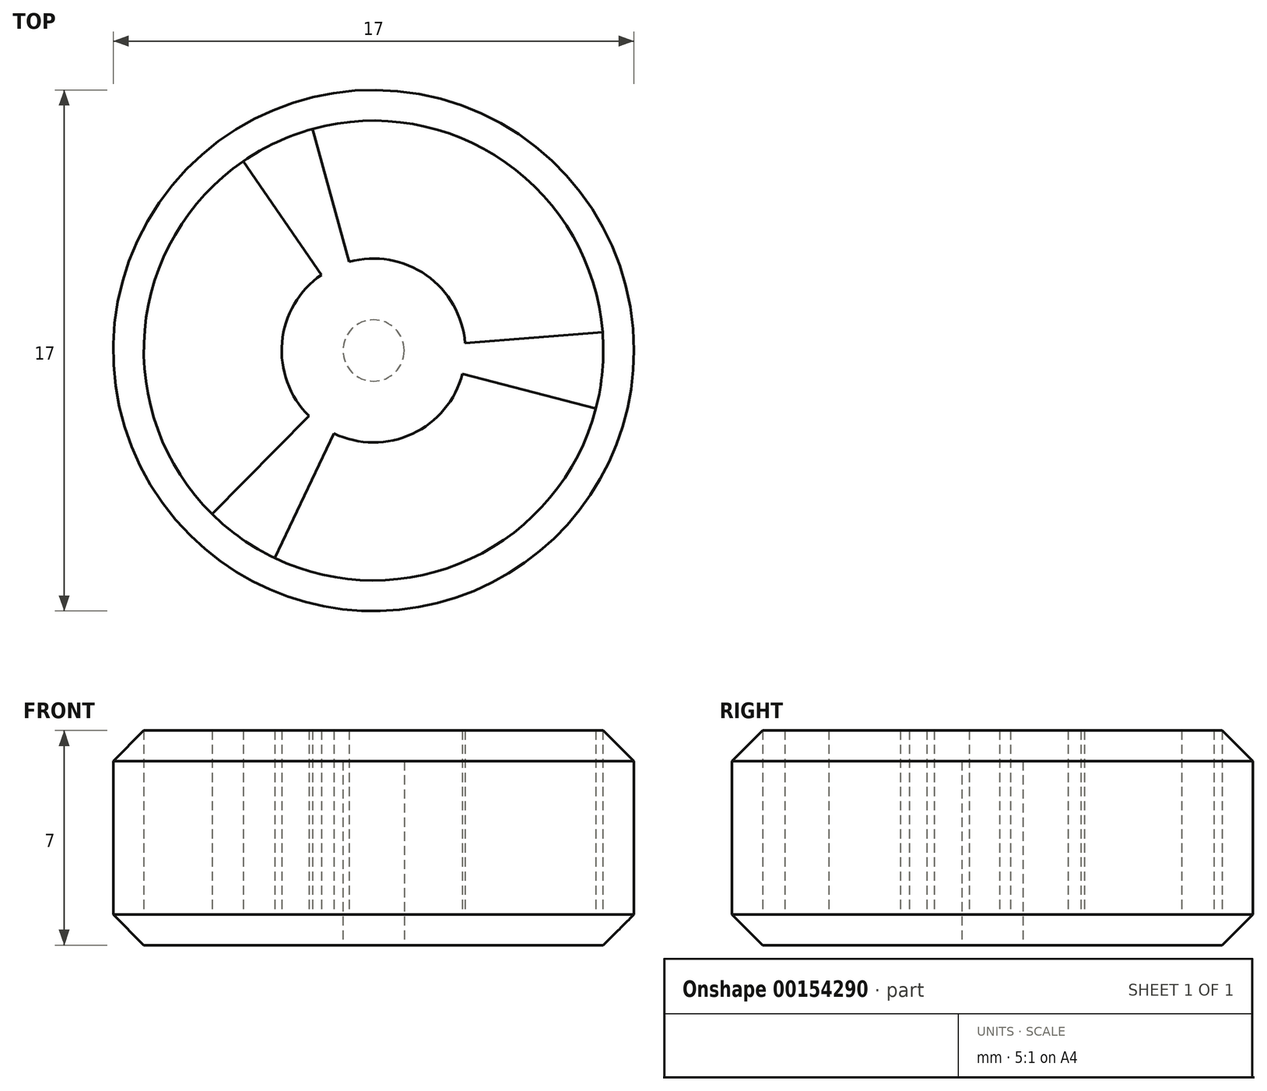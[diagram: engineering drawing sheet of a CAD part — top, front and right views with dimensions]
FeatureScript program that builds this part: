
annotation { "Feature Type Name" : "Feature", "Feature Type Description" : "" }
export const myFeature = defineFeature(function(context is Context, id is Id, definition is map)
    precondition{}
    {
        {
            var Q0;
            Q0=qCreatedBy(makeId("Top.planeOp"),FACE);
            var sketch = newSketch(context, id + "F0", { "sketchPlane" : qUnion([Q0])});
            skCircle(sketch, "E0", {"center": v(0, 0) * mm, "radius": 8.5 * mm});
            skCircle(sketch, "E1", {"center": v(0, 0) * mm, "radius": 1 * mm});
            skCircle(sketch, "E2", {"center": v(0, 0) * mm, "radius": 3 * mm});
            skLineSegment(sketch, "E3", {"start": v(0, 0) * mm, "end": v(-4.82, 7) * mm});
            skLineSegment(sketch, "E4", {"start": v(0, 0) * mm, "end": v(-2.25, 8.2) * mm});
            skPoint(sketch, "E5", {"position": v(-1.7, 2.47) * mm});
            skPoint(sketch, "E6", {"position": v(-0.8, 2.9) * mm});
            skLineSegment(sketch, "E7.1.0", {"start": v(0, 0) * mm, "end": v(-3.65, -7.68) * mm});
            skLineSegment(sketch, "E7.2.0", {"start": v(0, 0) * mm, "end": v(8.47, 0.68) * mm});
            skLineSegment(sketch, "E8.1.0", {"start": v(0, 0) * mm, "end": v(-5.97, -6.05) * mm});
            skLineSegment(sketch, "E8.2.0", {"start": v(0, 0) * mm, "end": v(8.22, -2.15) * mm});
            skCircle(sketch, "E9", {"center": v(0, 0) * mm, "radius": 7.5 * mm});
            skSolve(sketch);
        }
        {
            var Q0;
            {var subQ0=sQuery(id+"F0.wireOp",EDGE,"E7.1.0");var subQ1=sQuery(id+"F0.wireOp",EDGE,"E2");var subQ2=makeQuery(id+"F0.imprint","INTERSECT",VERTEX,{"derivedFrom":[subQ1,subQ0]});Q0=makeQuery(id+"F0.imprint","IMPRINT",FACE,{"disambiguationData":[TD([[makeQuery(id+"F0.imprint","IMPRINT",EDGE,{"disambiguationData":[TD([[subQ2,-1.0]])],"derivedFrom":subQ1}),-1.0]])]});}
            var Q1;
            {var subQ0=sQuery(id+"F0.wireOp",EDGE,"E3");var subQ1=sQuery(id+"F0.wireOp",EDGE,"E2");var subQ2=makeQuery(id+"F0.imprint","INTERSECT",VERTEX,{"derivedFrom":[subQ1,subQ0]});Q1=makeQuery(id+"F0.imprint","IMPRINT",FACE,{"disambiguationData":[TD([[makeQuery(id+"F0.imprint","IMPRINT",EDGE,{"disambiguationData":[TD([[subQ2,-1.0]])],"derivedFrom":subQ1}),-1.0]])]});}
            var Q2;
            {var subQ0=sQuery(id+"F0.wireOp",EDGE,"E7.2.0");var subQ1=sQuery(id+"F0.wireOp",EDGE,"E1");var subQ2=makeQuery(id+"F0.imprint","INTERSECT",VERTEX,{"derivedFrom":[subQ1,subQ0]});Q2=makeQuery(id+"F0.imprint","IMPRINT",FACE,{"disambiguationData":[TD([[makeQuery(id+"F0.imprint","IMPRINT",EDGE,{"disambiguationData":[TD([[subQ2,1.0]])],"derivedFrom":subQ1}),-1.0]])]});}
            var Q3;
            {var subQ0=sQuery(id+"F0.wireOp",EDGE,"E4");var subQ1=sQuery(id+"F0.wireOp",EDGE,"E2");var subQ2=makeQuery(id+"F0.imprint","INTERSECT",VERTEX,{"derivedFrom":[subQ1,subQ0]});Q3=makeQuery(id+"F0.imprint","IMPRINT",FACE,{"disambiguationData":[TD([[makeQuery(id+"F0.imprint","IMPRINT",EDGE,{"disambiguationData":[TD([[subQ2,-1.0]])],"derivedFrom":subQ1}),-1.0]])]});}
            var Q4;
            {var subQ0=sQuery(id+"F0.wireOp",EDGE,"E8.1.0");var subQ1=sQuery(id+"F0.wireOp",EDGE,"E2");var subQ2=makeQuery(id+"F0.imprint","INTERSECT",VERTEX,{"derivedFrom":[subQ1,subQ0]});Q4=makeQuery(id+"F0.imprint","IMPRINT",FACE,{"disambiguationData":[TD([[makeQuery(id+"F0.imprint","IMPRINT",EDGE,{"disambiguationData":[TD([[subQ2,-1.0]])],"derivedFrom":subQ1}),-1.0]])]});}
            var Q5;
            {var subQ0=sQuery(id+"F0.wireOp",EDGE,"E8.1.0");var subQ1=sQuery(id+"F0.wireOp",EDGE,"E1");var subQ2=makeQuery(id+"F0.imprint","INTERSECT",VERTEX,{"derivedFrom":[subQ1,subQ0]});Q5=makeQuery(id+"F0.imprint","IMPRINT",FACE,{"disambiguationData":[TD([[makeQuery(id+"F0.imprint","IMPRINT",EDGE,{"disambiguationData":[TD([[subQ2,-1.0]])],"derivedFrom":subQ1}),-1.0]])]});}
            var Q6;
            {var subQ0=sQuery(id+"F0.wireOp",EDGE,"E4");var subQ1=sQuery(id+"F0.wireOp",EDGE,"E1");var subQ2=makeQuery(id+"F0.imprint","INTERSECT",VERTEX,{"derivedFrom":[subQ1,subQ0]});Q6=makeQuery(id+"F0.imprint","IMPRINT",FACE,{"disambiguationData":[TD([[makeQuery(id+"F0.imprint","IMPRINT",EDGE,{"disambiguationData":[TD([[subQ2,-1.0]])],"derivedFrom":subQ1}),-1.0]])]});}
            var Q7;
            {var subQ0=sQuery(id+"F0.wireOp",EDGE,"E7.1.0");var subQ1=sQuery(id+"F0.wireOp",EDGE,"E1");var subQ2=makeQuery(id+"F0.imprint","INTERSECT",VERTEX,{"derivedFrom":[subQ1,subQ0]});Q7=makeQuery(id+"F0.imprint","IMPRINT",FACE,{"disambiguationData":[TD([[makeQuery(id+"F0.imprint","IMPRINT",EDGE,{"disambiguationData":[TD([[subQ2,-1.0]])],"derivedFrom":subQ1}),-1.0]])]});}
            var Q8;
            {var subQ0=sQuery(id+"F0.wireOp",EDGE,"E3");var subQ1=sQuery(id+"F0.wireOp",EDGE,"E1");var subQ2=makeQuery(id+"F0.imprint","INTERSECT",VERTEX,{"derivedFrom":[subQ1,subQ0]});Q8=makeQuery(id+"F0.imprint","IMPRINT",FACE,{"disambiguationData":[TD([[makeQuery(id+"F0.imprint","IMPRINT",EDGE,{"disambiguationData":[TD([[subQ2,-1.0]])],"derivedFrom":subQ1}),-1.0]])]});}
            var Q9;
            {var subQ0=sQuery(id+"F0.wireOp",EDGE,"E4");var subQ1=sQuery(id+"F0.wireOp",EDGE,"E2");var subQ2=makeQuery(id+"F0.imprint","INTERSECT",VERTEX,{"derivedFrom":[subQ1,subQ0]});Q9=makeQuery(id+"F0.imprint","IMPRINT",FACE,{"disambiguationData":[TD([[makeQuery(id+"F0.imprint","IMPRINT",EDGE,{"disambiguationData":[TD([[subQ2,1.0]])],"derivedFrom":subQ1}),-1.0]])]});}
            var Q10;
            {var subQ0=sQuery(id+"F0.wireOp",EDGE,"E4");var subQ1=sQuery(id+"F0.wireOp",EDGE,"E1");var subQ2=makeQuery(id+"F0.imprint","INTERSECT",VERTEX,{"derivedFrom":[subQ1,subQ0]});Q10=makeQuery(id+"F0.imprint","IMPRINT",FACE,{"disambiguationData":[TD([[makeQuery(id+"F0.imprint","IMPRINT",EDGE,{"disambiguationData":[TD([[subQ2,1.0]])],"derivedFrom":subQ1}),-1.0]])]});}
            var Q11;
            {var subQ0=sQuery(id+"F0.wireOp",EDGE,"E7.2.0");var subQ1=sQuery(id+"F0.wireOp",EDGE,"E2");var subQ2=makeQuery(id+"F0.imprint","INTERSECT",VERTEX,{"derivedFrom":[subQ1,subQ0]});Q11=makeQuery(id+"F0.imprint","IMPRINT",FACE,{"disambiguationData":[TD([[makeQuery(id+"F0.imprint","IMPRINT",EDGE,{"disambiguationData":[TD([[subQ2,1.0]])],"derivedFrom":subQ1}),-1.0]])]});}
            var Q12;
            {var subQ0=sQuery(id+"F0.wireOp",EDGE,"E4");var subQ1=sQuery(id+"F0.wireOp",EDGE,"E0");var subQ2=makeQuery(id+"F0.imprint","INTERSECT",VERTEX,{"derivedFrom":[subQ1,subQ0]});Q12=makeQuery(id+"F0.imprint","IMPRINT",FACE,{"disambiguationData":[TD([[makeQuery(id+"F0.imprint","IMPRINT",EDGE,{"disambiguationData":[TD([[subQ2,1.0]])],"derivedFrom":subQ1}),1.0]])]});}
            var Q13;
            {var subQ0=sQuery(id+"F0.wireOp",EDGE,"E3");var subQ1=sQuery(id+"F0.wireOp",EDGE,"E0");var subQ2=makeQuery(id+"F0.imprint","INTERSECT",VERTEX,{"derivedFrom":[subQ1,subQ0]});Q13=makeQuery(id+"F0.imprint","IMPRINT",FACE,{"disambiguationData":[TD([[makeQuery(id+"F0.imprint","IMPRINT",EDGE,{"disambiguationData":[TD([[subQ2,1.0]])],"derivedFrom":subQ1}),1.0]])]});}
            var Q14;
            {var subQ0=sQuery(id+"F0.wireOp",EDGE,"E3");var subQ1=sQuery(id+"F0.wireOp",EDGE,"E0");var subQ2=makeQuery(id+"F0.imprint","INTERSECT",VERTEX,{"derivedFrom":[subQ1,subQ0]});Q14=makeQuery(id+"F0.imprint","IMPRINT",FACE,{"disambiguationData":[TD([[makeQuery(id+"F0.imprint","IMPRINT",EDGE,{"disambiguationData":[TD([[subQ2,-1.0]])],"derivedFrom":subQ1}),1.0]])]});}
            var Q15;
            {var subQ0=sQuery(id+"F0.wireOp",EDGE,"E7.1.0");var subQ1=sQuery(id+"F0.wireOp",EDGE,"E0");var subQ2=makeQuery(id+"F0.imprint","INTERSECT",VERTEX,{"derivedFrom":[subQ1,subQ0]});Q15=makeQuery(id+"F0.imprint","IMPRINT",FACE,{"disambiguationData":[TD([[makeQuery(id+"F0.imprint","IMPRINT",EDGE,{"disambiguationData":[TD([[subQ2,1.0]])],"derivedFrom":subQ1}),1.0]])]});}
            var Q16;
            {var subQ0=sQuery(id+"F0.wireOp",EDGE,"E7.1.0");var subQ1=sQuery(id+"F0.wireOp",EDGE,"E0");var subQ2=makeQuery(id+"F0.imprint","INTERSECT",VERTEX,{"derivedFrom":[subQ1,subQ0]});Q16=makeQuery(id+"F0.imprint","IMPRINT",FACE,{"disambiguationData":[TD([[makeQuery(id+"F0.imprint","IMPRINT",EDGE,{"disambiguationData":[TD([[subQ2,-1.0]])],"derivedFrom":subQ1}),1.0]])]});}
            var Q17;
            {var subQ0=sQuery(id+"F0.wireOp",EDGE,"E7.2.0");var subQ1=sQuery(id+"F0.wireOp",EDGE,"E0");var subQ2=makeQuery(id+"F0.imprint","INTERSECT",VERTEX,{"derivedFrom":[subQ1,subQ0]});Q17=makeQuery(id+"F0.imprint","IMPRINT",FACE,{"disambiguationData":[TD([[makeQuery(id+"F0.imprint","IMPRINT",EDGE,{"disambiguationData":[TD([[subQ2,1.0]])],"derivedFrom":subQ1}),1.0]])]});}
            extrude(context, id + "F1", {"entities" : qUnion([Q0, Q1, Q2, Q3, Q4, Q5, Q6, Q7, Q8, Q9, Q10, Q11, Q12, Q13, Q14, Q15, Q16, Q17]), "depth" : 1 * mm});
        }
        {
            var Q0;
            {var subQ0=sQuery(id+"F0.wireOp",EDGE,"E3");var subQ1=sQuery(id+"F0.wireOp",EDGE,"E0");var subQ2=makeQuery(id+"F0.imprint","INTERSECT",VERTEX,{"derivedFrom":[subQ1,subQ0]});Q0=makeQuery(id+"F0.imprint","IMPRINT",FACE,{"disambiguationData":[TD([[makeQuery(id+"F0.imprint","IMPRINT",EDGE,{"disambiguationData":[TD([[subQ2,-1.0]])],"derivedFrom":subQ1}),1.0]])]});}
            var Q1;
            {var subQ0=sQuery(id+"F0.wireOp",EDGE,"E7.1.0");var subQ1=sQuery(id+"F0.wireOp",EDGE,"E0");var subQ2=makeQuery(id+"F0.imprint","INTERSECT",VERTEX,{"derivedFrom":[subQ1,subQ0]});Q1=makeQuery(id+"F0.imprint","IMPRINT",FACE,{"disambiguationData":[TD([[makeQuery(id+"F0.imprint","IMPRINT",EDGE,{"disambiguationData":[TD([[subQ2,1.0]])],"derivedFrom":subQ1}),1.0]])]});}
            var Q2;
            {var subQ0=sQuery(id+"F0.wireOp",EDGE,"E7.1.0");var subQ1=sQuery(id+"F0.wireOp",EDGE,"E0");var subQ2=makeQuery(id+"F0.imprint","INTERSECT",VERTEX,{"derivedFrom":[subQ1,subQ0]});Q2=makeQuery(id+"F0.imprint","IMPRINT",FACE,{"disambiguationData":[TD([[makeQuery(id+"F0.imprint","IMPRINT",EDGE,{"disambiguationData":[TD([[subQ2,-1.0]])],"derivedFrom":subQ1}),1.0]])]});}
            var Q3;
            {var subQ0=sQuery(id+"F0.wireOp",EDGE,"E7.2.0");var subQ1=sQuery(id+"F0.wireOp",EDGE,"E0");var subQ2=makeQuery(id+"F0.imprint","INTERSECT",VERTEX,{"derivedFrom":[subQ1,subQ0]});Q3=makeQuery(id+"F0.imprint","IMPRINT",FACE,{"disambiguationData":[TD([[makeQuery(id+"F0.imprint","IMPRINT",EDGE,{"disambiguationData":[TD([[subQ2,1.0]])],"derivedFrom":subQ1}),1.0]])]});}
            var Q4;
            {var subQ0=sQuery(id+"F0.wireOp",EDGE,"E4");var subQ1=sQuery(id+"F0.wireOp",EDGE,"E0");var subQ2=makeQuery(id+"F0.imprint","INTERSECT",VERTEX,{"derivedFrom":[subQ1,subQ0]});Q4=makeQuery(id+"F0.imprint","IMPRINT",FACE,{"disambiguationData":[TD([[makeQuery(id+"F0.imprint","IMPRINT",EDGE,{"disambiguationData":[TD([[subQ2,1.0]])],"derivedFrom":subQ1}),1.0]])]});}
            var Q5;
            {var subQ0=sQuery(id+"F0.wireOp",EDGE,"E3");var subQ1=sQuery(id+"F0.wireOp",EDGE,"E0");var subQ2=makeQuery(id+"F0.imprint","INTERSECT",VERTEX,{"derivedFrom":[subQ1,subQ0]});Q5=makeQuery(id+"F0.imprint","IMPRINT",FACE,{"disambiguationData":[TD([[makeQuery(id+"F0.imprint","IMPRINT",EDGE,{"disambiguationData":[TD([[subQ2,1.0]])],"derivedFrom":subQ1}),1.0]])]});}
            var Q6;
            {var subQ0=sQuery(id+"F0.wireOp",EDGE,"E4");var subQ1=sQuery(id+"F0.wireOp",EDGE,"E1");var subQ2=makeQuery(id+"F0.imprint","INTERSECT",VERTEX,{"derivedFrom":[subQ1,subQ0]});Q6=makeQuery(id+"F0.imprint","IMPRINT",FACE,{"disambiguationData":[TD([[makeQuery(id+"F0.imprint","IMPRINT",EDGE,{"disambiguationData":[TD([[subQ2,-1.0]])],"derivedFrom":subQ1}),-1.0]])]});}
            var Q7;
            {var subQ0=sQuery(id+"F0.wireOp",EDGE,"E3");var subQ1=sQuery(id+"F0.wireOp",EDGE,"E1");var subQ2=makeQuery(id+"F0.imprint","INTERSECT",VERTEX,{"derivedFrom":[subQ1,subQ0]});Q7=makeQuery(id+"F0.imprint","IMPRINT",FACE,{"disambiguationData":[TD([[makeQuery(id+"F0.imprint","IMPRINT",EDGE,{"disambiguationData":[TD([[subQ2,-1.0]])],"derivedFrom":subQ1}),-1.0]])]});}
            var Q8;
            {var subQ0=sQuery(id+"F0.wireOp",EDGE,"E8.1.0");var subQ1=sQuery(id+"F0.wireOp",EDGE,"E1");var subQ2=makeQuery(id+"F0.imprint","INTERSECT",VERTEX,{"derivedFrom":[subQ1,subQ0]});Q8=makeQuery(id+"F0.imprint","IMPRINT",FACE,{"disambiguationData":[TD([[makeQuery(id+"F0.imprint","IMPRINT",EDGE,{"disambiguationData":[TD([[subQ2,-1.0]])],"derivedFrom":subQ1}),-1.0]])]});}
            var Q9;
            {var subQ0=sQuery(id+"F0.wireOp",EDGE,"E7.1.0");var subQ1=sQuery(id+"F0.wireOp",EDGE,"E1");var subQ2=makeQuery(id+"F0.imprint","INTERSECT",VERTEX,{"derivedFrom":[subQ1,subQ0]});Q9=makeQuery(id+"F0.imprint","IMPRINT",FACE,{"disambiguationData":[TD([[makeQuery(id+"F0.imprint","IMPRINT",EDGE,{"disambiguationData":[TD([[subQ2,-1.0]])],"derivedFrom":subQ1}),-1.0]])]});}
            var Q10;
            {var subQ0=sQuery(id+"F0.wireOp",EDGE,"E7.2.0");var subQ1=sQuery(id+"F0.wireOp",EDGE,"E1");var subQ2=makeQuery(id+"F0.imprint","INTERSECT",VERTEX,{"derivedFrom":[subQ1,subQ0]});Q10=makeQuery(id+"F0.imprint","IMPRINT",FACE,{"disambiguationData":[TD([[makeQuery(id+"F0.imprint","IMPRINT",EDGE,{"disambiguationData":[TD([[subQ2,1.0]])],"derivedFrom":subQ1}),-1.0]])]});}
            var Q11;
            {var subQ0=sQuery(id+"F0.wireOp",EDGE,"E4");var subQ1=sQuery(id+"F0.wireOp",EDGE,"E1");var subQ2=makeQuery(id+"F0.imprint","INTERSECT",VERTEX,{"derivedFrom":[subQ1,subQ0]});Q11=makeQuery(id+"F0.imprint","IMPRINT",FACE,{"disambiguationData":[TD([[makeQuery(id+"F0.imprint","IMPRINT",EDGE,{"disambiguationData":[TD([[subQ2,1.0]])],"derivedFrom":subQ1}),-1.0]])]});}
            var Q12;
            {var subQ0=sQuery(id+"F0.wireOp",EDGE,"E4");var subQ1=sQuery(id+"F0.wireOp",EDGE,"E2");var subQ2=makeQuery(id+"F0.imprint","INTERSECT",VERTEX,{"derivedFrom":[subQ1,subQ0]});Q12=makeQuery(id+"F0.imprint","IMPRINT",FACE,{"disambiguationData":[TD([[makeQuery(id+"F0.imprint","IMPRINT",EDGE,{"disambiguationData":[TD([[subQ2,-1.0]])],"derivedFrom":subQ1}),-1.0]])]});}
            var Q13;
            {var subQ0=sQuery(id+"F0.wireOp",EDGE,"E8.1.0");var subQ1=sQuery(id+"F0.wireOp",EDGE,"E2");var subQ2=makeQuery(id+"F0.imprint","INTERSECT",VERTEX,{"derivedFrom":[subQ1,subQ0]});Q13=makeQuery(id+"F0.imprint","IMPRINT",FACE,{"disambiguationData":[TD([[makeQuery(id+"F0.imprint","IMPRINT",EDGE,{"disambiguationData":[TD([[subQ2,-1.0]])],"derivedFrom":subQ1}),-1.0]])]});}
            var Q14;
            {var subQ0=sQuery(id+"F0.wireOp",EDGE,"E7.2.0");var subQ1=sQuery(id+"F0.wireOp",EDGE,"E2");var subQ2=makeQuery(id+"F0.imprint","INTERSECT",VERTEX,{"derivedFrom":[subQ1,subQ0]});Q14=makeQuery(id+"F0.imprint","IMPRINT",FACE,{"disambiguationData":[TD([[makeQuery(id+"F0.imprint","IMPRINT",EDGE,{"disambiguationData":[TD([[subQ2,1.0]])],"derivedFrom":subQ1}),-1.0]])]});}
            var Q15;
            {var subQ0=sQuery(id+"F0.wireOp",EDGE,"E4");var subQ1=sQuery(id+"F0.wireOp",EDGE,"E1");var subQ2=makeQuery(id+"F0.imprint","INTERSECT",VERTEX,{"derivedFrom":[subQ1,subQ0]});Q15=makeQuery(id+"F0.imprint","IMPRINT",FACE,{"disambiguationData":[TD([[makeQuery(id+"F0.imprint","IMPRINT",EDGE,{"disambiguationData":[TD([[subQ2,-1.0]])],"derivedFrom":subQ1}),1.0]])]});}
            var Q16;
            {var subQ0=sQuery(id+"F0.wireOp",EDGE,"E3");var subQ1=sQuery(id+"F0.wireOp",EDGE,"E1");var subQ2=makeQuery(id+"F0.imprint","INTERSECT",VERTEX,{"derivedFrom":[subQ1,subQ0]});Q16=makeQuery(id+"F0.imprint","IMPRINT",FACE,{"disambiguationData":[TD([[makeQuery(id+"F0.imprint","IMPRINT",EDGE,{"disambiguationData":[TD([[subQ2,-1.0]])],"derivedFrom":subQ1}),1.0]])]});}
            var Q17;
            {var subQ0=sQuery(id+"F0.wireOp",EDGE,"E8.1.0");var subQ1=sQuery(id+"F0.wireOp",EDGE,"E1");var subQ2=makeQuery(id+"F0.imprint","INTERSECT",VERTEX,{"derivedFrom":[subQ1,subQ0]});Q17=makeQuery(id+"F0.imprint","IMPRINT",FACE,{"disambiguationData":[TD([[makeQuery(id+"F0.imprint","IMPRINT",EDGE,{"disambiguationData":[TD([[subQ2,-1.0]])],"derivedFrom":subQ1}),1.0]])]});}
            var Q18;
            {var subQ0=sQuery(id+"F0.wireOp",EDGE,"E7.1.0");var subQ1=sQuery(id+"F0.wireOp",EDGE,"E1");var subQ2=makeQuery(id+"F0.imprint","INTERSECT",VERTEX,{"derivedFrom":[subQ1,subQ0]});Q18=makeQuery(id+"F0.imprint","IMPRINT",FACE,{"disambiguationData":[TD([[makeQuery(id+"F0.imprint","IMPRINT",EDGE,{"disambiguationData":[TD([[subQ2,-1.0]])],"derivedFrom":subQ1}),1.0]])]});}
            var Q19;
            {var subQ0=sQuery(id+"F0.wireOp",EDGE,"E7.2.0");var subQ1=sQuery(id+"F0.wireOp",EDGE,"E1");var subQ2=makeQuery(id+"F0.imprint","INTERSECT",VERTEX,{"derivedFrom":[subQ1,subQ0]});Q19=makeQuery(id+"F0.imprint","IMPRINT",FACE,{"disambiguationData":[TD([[makeQuery(id+"F0.imprint","IMPRINT",EDGE,{"disambiguationData":[TD([[subQ2,1.0]])],"derivedFrom":subQ1}),1.0]])]});}
            var Q20;
            {var subQ0=sQuery(id+"F0.wireOp",EDGE,"E4");var subQ1=sQuery(id+"F0.wireOp",EDGE,"E1");var subQ2=makeQuery(id+"F0.imprint","INTERSECT",VERTEX,{"derivedFrom":[subQ1,subQ0]});Q20=makeQuery(id+"F0.imprint","IMPRINT",FACE,{"disambiguationData":[TD([[makeQuery(id+"F0.imprint","IMPRINT",EDGE,{"disambiguationData":[TD([[subQ2,1.0]])],"derivedFrom":subQ1}),1.0]])]});}
            extrude(context, id + "F2", {"entities" : qUnion([Q0, Q1, Q2, Q3, Q4, Q5, Q6, Q7, Q8, Q9, Q10, Q11, Q12, Q13, Q14, Q15, Q16, Q17, Q18, Q19, Q20]), "operationType" : NewBodyOperationType.ADD, "depth" : 7 * mm});
        }
        {
            var Q0;
            {var subQ0=sQuery(id+"F0.wireOp",EDGE,"E7.1.0");var subQ1=sQuery(id+"F0.wireOp",EDGE,"E1");var subQ2=makeQuery(id+"F0.imprint","INTERSECT",VERTEX,{"derivedFrom":[subQ1,subQ0]});Q0=makeQuery(id+"F0.imprint","IMPRINT",FACE,{"disambiguationData":[TD([[makeQuery(id+"F0.imprint","IMPRINT",EDGE,{"disambiguationData":[TD([[subQ2,-1.0]])],"derivedFrom":subQ1}),1.0]])]});}
            var Q1;
            {var subQ0=sQuery(id+"F0.wireOp",EDGE,"E7.2.0");var subQ1=sQuery(id+"F0.wireOp",EDGE,"E1");var subQ2=makeQuery(id+"F0.imprint","INTERSECT",VERTEX,{"derivedFrom":[subQ1,subQ0]});Q1=makeQuery(id+"F0.imprint","IMPRINT",FACE,{"disambiguationData":[TD([[makeQuery(id+"F0.imprint","IMPRINT",EDGE,{"disambiguationData":[TD([[subQ2,1.0]])],"derivedFrom":subQ1}),1.0]])]});}
            var Q2;
            {var subQ0=sQuery(id+"F0.wireOp",EDGE,"E4");var subQ1=sQuery(id+"F0.wireOp",EDGE,"E1");var subQ2=makeQuery(id+"F0.imprint","INTERSECT",VERTEX,{"derivedFrom":[subQ1,subQ0]});Q2=makeQuery(id+"F0.imprint","IMPRINT",FACE,{"disambiguationData":[TD([[makeQuery(id+"F0.imprint","IMPRINT",EDGE,{"disambiguationData":[TD([[subQ2,1.0]])],"derivedFrom":subQ1}),1.0]])]});}
            var Q3;
            {var subQ0=sQuery(id+"F0.wireOp",EDGE,"E3");var subQ1=sQuery(id+"F0.wireOp",EDGE,"E1");var subQ2=makeQuery(id+"F0.imprint","INTERSECT",VERTEX,{"derivedFrom":[subQ1,subQ0]});Q3=makeQuery(id+"F0.imprint","IMPRINT",FACE,{"disambiguationData":[TD([[makeQuery(id+"F0.imprint","IMPRINT",EDGE,{"disambiguationData":[TD([[subQ2,-1.0]])],"derivedFrom":subQ1}),1.0]])]});}
            var Q4;
            {var subQ0=sQuery(id+"F0.wireOp",EDGE,"E8.1.0");var subQ1=sQuery(id+"F0.wireOp",EDGE,"E1");var subQ2=makeQuery(id+"F0.imprint","INTERSECT",VERTEX,{"derivedFrom":[subQ1,subQ0]});Q4=makeQuery(id+"F0.imprint","IMPRINT",FACE,{"disambiguationData":[TD([[makeQuery(id+"F0.imprint","IMPRINT",EDGE,{"disambiguationData":[TD([[subQ2,-1.0]])],"derivedFrom":subQ1}),1.0]])]});}
            var Q5;
            {var subQ0=sQuery(id+"F0.wireOp",EDGE,"E4");var subQ1=sQuery(id+"F0.wireOp",EDGE,"E1");var subQ2=makeQuery(id+"F0.imprint","INTERSECT",VERTEX,{"derivedFrom":[subQ1,subQ0]});Q5=makeQuery(id+"F0.imprint","IMPRINT",FACE,{"disambiguationData":[TD([[makeQuery(id+"F0.imprint","IMPRINT",EDGE,{"disambiguationData":[TD([[subQ2,-1.0]])],"derivedFrom":subQ1}),1.0]])]});}
            extrude(context, id + "F3", {"entities" : qUnion([Q0, Q1, Q2, Q3, Q4, Q5]), "operationType" : NewBodyOperationType.REMOVE, "depth" : 6 * mm});
        }
        {
            var Q0;
            Q0=makeQuery(id+"F2.opExtrude","CAP_EDGE",EDGE,{"disambiguationData":[OSD([sQuery(id+"F0.wireOp",EDGE,"E0")])],"isStart":false});
            chamfer(context, id + "F4", {"entities" : qUnion([Q0]), "width" : 1 * mm, "tangentPropagation" : true});
        }
        {
            var Q0;
            Q0=makeQuery(id+"F1.opExtrude","CAP_EDGE",EDGE,{"disambiguationData":[OSD([sQuery(id+"F0.wireOp",EDGE,"E0")])],"isStart":true});
            chamfer(context, id + "F5", {"entities" : qUnion([Q0]), "width" : 1 * mm, "tangentPropagation" : true});
        }
    });
